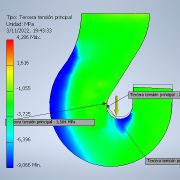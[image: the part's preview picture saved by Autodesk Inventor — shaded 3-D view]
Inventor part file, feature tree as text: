
AUTODESK INVENTOR PART (.ipt)
format: ipt  version: 2020.5 (Build 245400000, 400)  size: 192,000 bytes
history: native  units: mm
features: extrude x1, sketch x1
ambient origin geometry x8: Origin, YZ Plane, XZ Plane, XY Plane, X Axis, Y Axis, Z Axis, Center Point
bodies: Body1 (feature_tree)
feature tree (2):
  extrude  "Extrusión2"  Depth=52.0mm
  sketch  "Boceto1"  dims[d0=70.0mm d1=52.0mm d2=5.0mm d3=52.0mm d4=100.0mm d5=15.0mm d7=17.0mm d8=10.051676mm d9=54.787405mm d10=40.582091mm d11=52.0mm d14=37.0mm d15=10.0mm d16=52.0mm d17=40.0mm d18=0.0mm]
